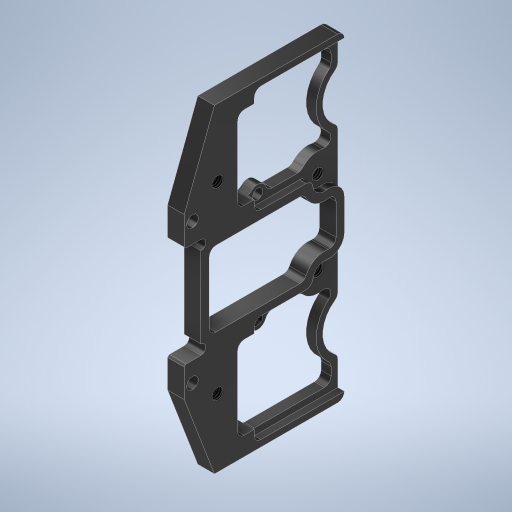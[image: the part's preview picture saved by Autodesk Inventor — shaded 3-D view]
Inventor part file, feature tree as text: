
AUTODESK INVENTOR PART (.ipt)
format: ipt  version: 2024.2 (Build 282272000, 272)  size: 473,088 bytes
history: native  units: mm
features: extrude x2, hole x2, other x1, mirror x1, chamfer x1, sketch x1
ambient origin geometry x8: Origin, YZ Plane, XZ Plane, XY Plane, X Axis, Y Axis, Z Axis, Center Point
bodies: Solid1 (feature_tree)
feature tree (8):
  other  "KneeFrameBasis.ipt"
  extrude  "Extrusion1"  Depth=5.0mm TaperAngle=0.0deg
  extrude  "Extrusion2"  Depth=2.0mm TaperAngle=0.0deg
  hole  "Phi3.1"  [1 undecoded]
  hole  "Phi3.5"  [1 undecoded]
  mirror  "Mirror1"
  chamfer  "C0.5"  Distance=0.5mm Angle=45.0deg
  sketch  "Sketch1"  dims[d0=10.0mm d1=5.0mm d2=0.0mm d3=2.0mm d4=0.0mm d7=0.0mm d8=0.0mm d9=3.242mm d10=8.0mm d11=4.0mm d12=2.0mm d13=90.0deg d14=8.0mm d15=20.594885mm d16=3.1mm d17=8.0mm d18=4.0mm d19=2.0mm d20=90.0deg d21=8.0mm d22=20.594885mm d23=3.5mm d24=6.0mm d25=4.0mm d26=2.0mm d27=90.0deg d28=8.0mm d29=20.594885mm d30=2.0mm d38=0.5mm d39=2.0mm d40=45.0deg]
note: 2 required parameter values undecoded (feature->parameter linkage not recoverable at this tier; creation-order binding heuristic only, values carry confidence <= 0.55)
